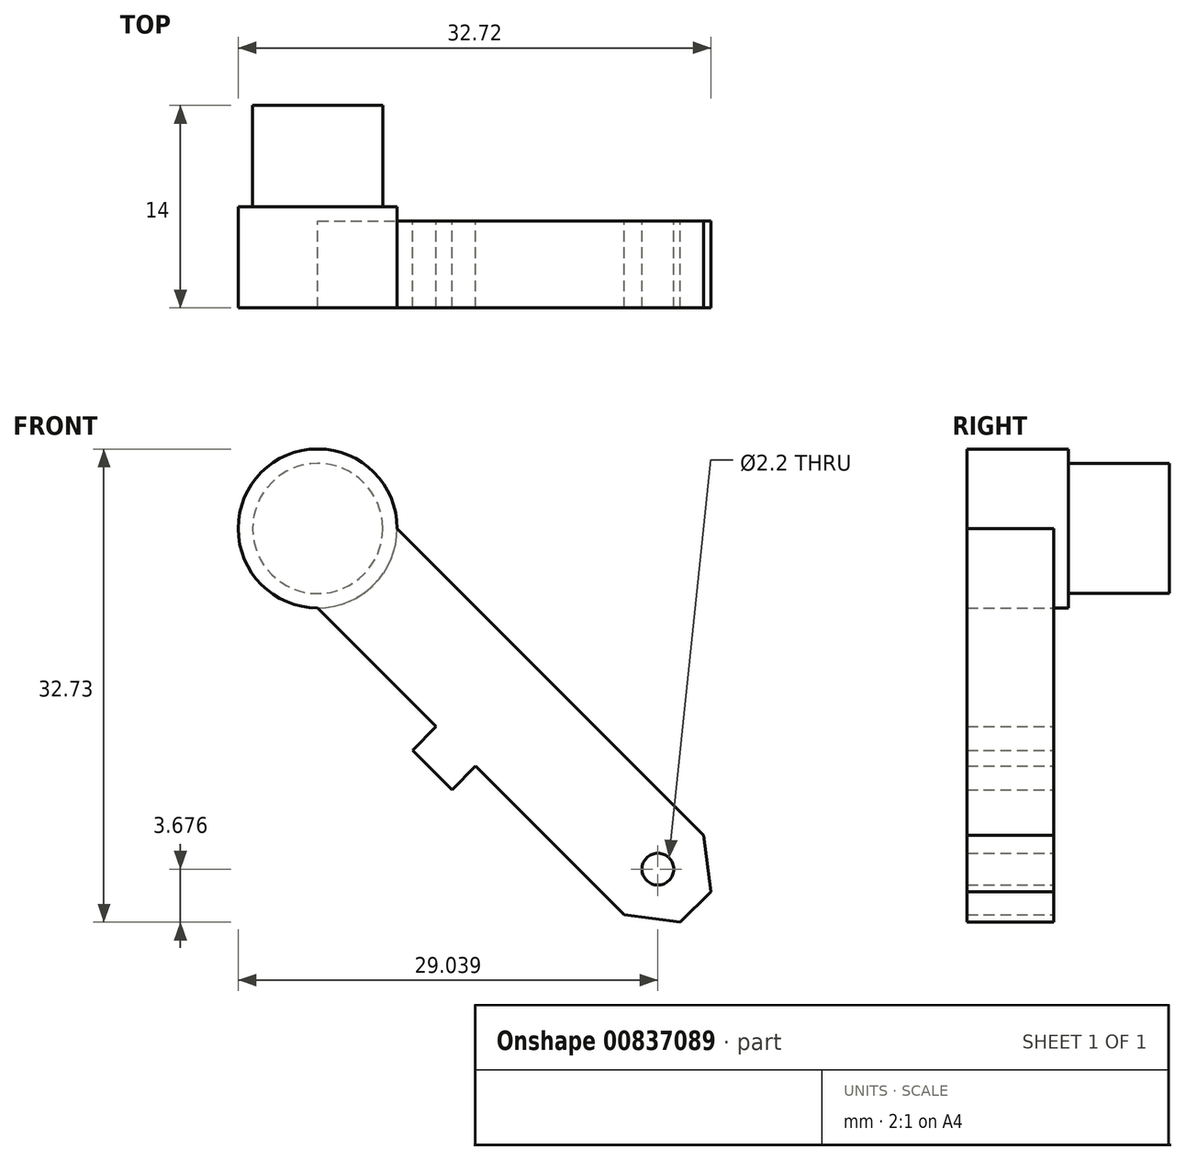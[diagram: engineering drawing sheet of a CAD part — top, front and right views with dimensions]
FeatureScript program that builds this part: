
annotation { "Feature Type Name" : "Feature", "Feature Type Description" : "" }
export const myFeature = defineFeature(function(context is Context, id is Id, definition is map)
    precondition{}
    {
        {
            var Q0;
            Q0=qCreatedBy(makeId("Front.planeOp"),FACE);
            var sketch = newSketch(context, id + "F0", { "sketchPlane" : qUnion([Q0])});
            skCircle(sketch, "E0", {"center": v(0, 0) * mm, "radius": 4.5 * mm});
            skCircle(sketch, "E1", {"center": v(0, 0) * mm, "radius": 13 * mm, "construction": true});
            skCircle(sketch, "E2", {"center": v(0, 0) * mm, "radius": 5.5 * mm});
            skLineSegment(sketch, "E3", {"start": v(0, -5.5) * mm, "end": v(21.21, -26.71) * mm});
            skLineSegment(sketch, "E4", {"start": v(21.21, -26.71) * mm, "end": v(25.1, -27.23) * mm});
            skLineSegment(sketch, "E5", {"start": v(25.1, -27.23) * mm, "end": v(27.22, -25.11) * mm});
            skLineSegment(sketch, "E6", {"start": v(27.22, -25.11) * mm, "end": v(26.71, -21.21) * mm});
            skLineSegment(sketch, "E7", {"start": v(26.71, -21.21) * mm, "end": v(5.5, 0) * mm});
            skCircle(sketch, "E8", {"center": v(23.54, -23.55) * mm, "radius": 1.1 * mm});
            skLineSegment(sketch, "E9", {"start": v(8.2, -13.7) * mm, "end": v(6.56, -15.33) * mm});
            skLineSegment(sketch, "E10", {"start": v(6.56, -15.33) * mm, "end": v(9.3, -18.07) * mm});
            skLineSegment(sketch, "E11", {"start": v(9.3, -18.07) * mm, "end": v(10.93, -16.43) * mm});
            skSolve(sketch);
        }
        {
            var Q0;
            Q0=makeQuery(id+"F0.imprint","IMPRINT",FACE,{"disambiguationData":[TD([[makeQuery(id+"F0.imprint","IMPRINT",EDGE,{"derivedFrom":sQuery(id+"F0.wireOp",EDGE,"E0")}),1.0]])]});
            var Q1;
            Q1=makeQuery(id+"F0.imprint","IMPRINT",FACE,{"disambiguationData":[TD([[makeQuery(id+"F0.imprint","IMPRINT",EDGE,{"derivedFrom":sQuery(id+"F0.wireOp",EDGE,"E0")}),-1.0]])]});
            var Q2;
            {var subQ0=sQuery(id+"F0.wireOp",EDGE,"E4");Q2=makeQuery(id+"F0.imprint","IMPRINT",FACE,{"disambiguationData":[TD([[makeQuery(id+"F0.imprint","IMPRINT",EDGE,{"derivedFrom":subQ0}),1.0]])]});}
            var Q3;
            {var subQ0=sQuery(id+"F0.wireOp",EDGE,"E9");Q3=makeQuery(id+"F0.imprint","IMPRINT",FACE,{"disambiguationData":[TD([[makeQuery(id+"F0.imprint","IMPRINT",EDGE,{"derivedFrom":subQ0}),1.0]])]});}
            extrude(context, id + "F1", {"entities" : qUnion([Q0, Q1, Q2, Q3]), "depth" : 6 * mm, "offsetDistance" : 25 * mm});
        }
        {
            var Q0;
            Q0=makeQuery(id+"F0.imprint","IMPRINT",FACE,{"disambiguationData":[TD([[makeQuery(id+"F0.imprint","IMPRINT",EDGE,{"derivedFrom":sQuery(id+"F0.wireOp",EDGE,"E0")}),-1.0]])]});
            var Q1;
            Q1=makeQuery(id+"F0.imprint","IMPRINT",FACE,{"disambiguationData":[TD([[makeQuery(id+"F0.imprint","IMPRINT",EDGE,{"derivedFrom":sQuery(id+"F0.wireOp",EDGE,"E0")}),1.0]])]});
            extrude(context, id + "F2", {"entities" : qUnion([Q0, Q1]), "operationType" : NewBodyOperationType.ADD, "oppositeDirection" : true, "depth" : 1 * mm, "offsetDistance" : 25 * mm});
        }
        {
            var Q0;
            Q0=makeQuery(id+"F0.imprint","IMPRINT",FACE,{"disambiguationData":[TD([[makeQuery(id+"F0.imprint","IMPRINT",EDGE,{"derivedFrom":sQuery(id+"F0.wireOp",EDGE,"E0")}),1.0]])]});
            extrude(context, id + "F3", {"entities" : qUnion([Q0]), "operationType" : NewBodyOperationType.ADD, "oppositeDirection" : true, "depth" : 8 * mm, "offsetDistance" : 25 * mm});
        }
    });
